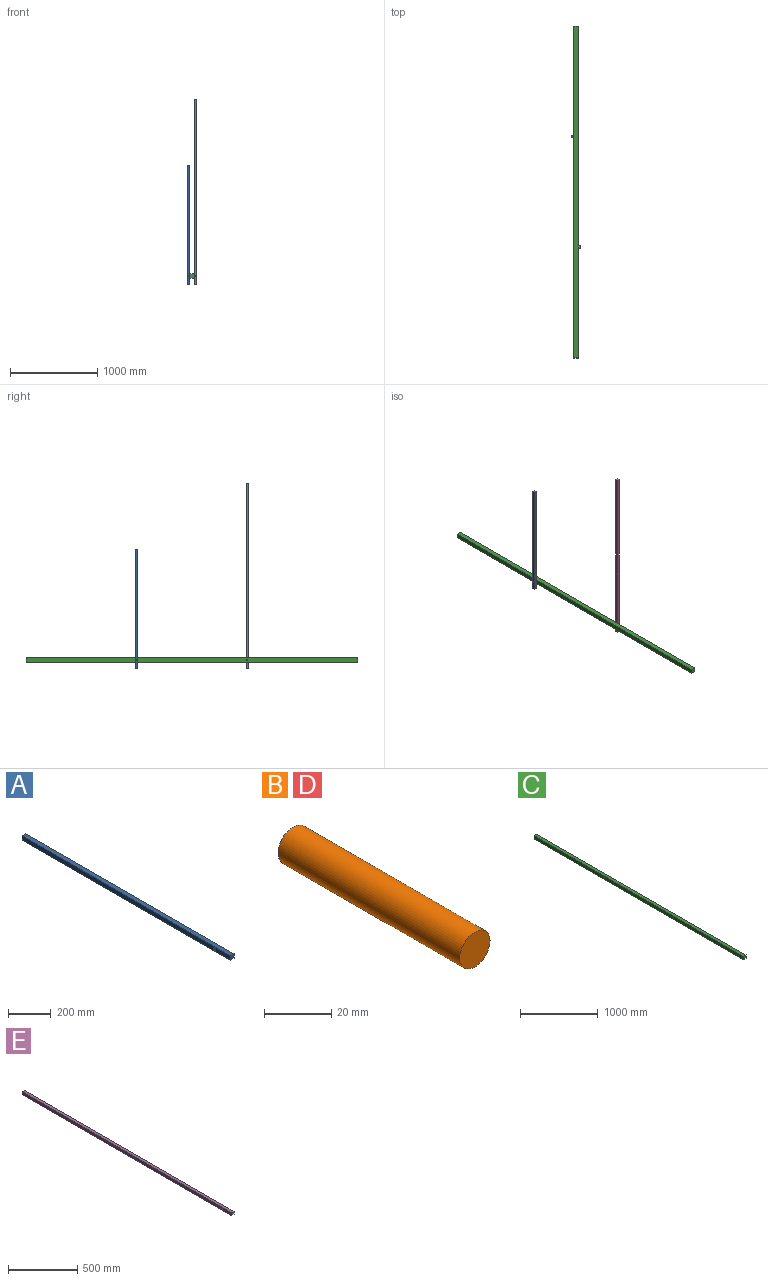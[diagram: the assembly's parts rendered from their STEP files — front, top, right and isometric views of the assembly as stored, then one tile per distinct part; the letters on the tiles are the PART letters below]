
ASSEMBLY  parts=5 mates=9
PART A: 7 faces, bbox 25.4x1371.6x25.4 mm
  f0: plane 1371.6x25.4mm, normal (0,0,1), area 34838.6mm2, adj f1,f3,f4,f5
  f1: plane 1371.6x25.4mm, normal (-1,0,0), area 34695.7mm2, adj f0,f2,f4,f5,f6
  f2: plane 1371.6x25.4mm, normal (0,0,-1), area 34838.6mm2, adj f1,f3,f4,f5
  f3: plane 1371.6x25.4mm, normal (1,0,0), area 34695.7mm2, adj f0,f2,f4,f5,f6
  f4: plane 25.4x25.4mm, normal (0,-1,0), area 645.2mm2, adj f0,f1,f2,f3
  f5: plane 25.4x25.4mm, normal (0,1,0), area 645.2mm2, adj f0,f1,f2,f3
  f6: cylinder r=6.75mm len=25.4mm, axis (1,0,0), area 1076.7mm2, adj f1,f3
PART B: 3 faces, bbox 12.7x76.2x12.7 mm
  f0: cylinder r=6.35mm len=76.2mm, axis (0,1,0), area 3040.2mm2, adj f1,f2
  f1: plane 12.7x12.7mm, normal (0,-1,0), area 126.7mm2, adj f0
  f2: plane 12.7x12.7mm, normal (0,1,0), area 126.7mm2, adj f0
PART C: 8 faces, bbox 50.8x3810x50.8 mm
  f0: plane 3810x50.8mm, normal (-1,0,0), area 193262mm2, adj f1,f3,f4,f5,f6,f7
  f1: plane 3810x50.8mm, normal (0,0,-1), area 193548mm2, adj f0,f2,f4,f5
  f2: plane 3810x50.8mm, normal (1,0,0), area 193262mm2, adj f1,f3,f4,f5,f6,f7
  f3: plane 3810x50.8mm, normal (0,0,1), area 193548mm2, adj f0,f2,f4,f5
  f4: plane 50.8x50.8mm, normal (0,-1,0), area 2580.6mm2, adj f0,f1,f2,f3
  f5: plane 50.8x50.8mm, normal (0,1,0), area 2580.6mm2, adj f0,f1,f2,f3
  f6: cylinder r=6.75mm len=50.8mm, axis (1,0,0), area 2153.3mm2, adj f0,f2
  f7: cylinder r=6.75mm len=50.8mm, axis (1,0,0), area 2153.3mm2, adj f0,f2
PART D: same geometry as B
PART E: 7 faces, bbox 25.4x2133.6x25.4 mm
  f0: plane 2133.6x25.4mm, normal (0,0,1), area 54193.4mm2, adj f1,f3,f4,f5
  f1: plane 2133.6x25.4mm, normal (-1,0,0), area 54050.5mm2, adj f0,f2,f4,f5,f6
  f2: plane 2133.6x25.4mm, normal (0,0,-1), area 54193.4mm2, adj f1,f3,f4,f5
  f3: plane 2133.6x25.4mm, normal (1,0,0), area 54050.5mm2, adj f0,f2,f4,f5,f6
  f4: plane 25.4x25.4mm, normal (0,-1,0), area 645.2mm2, adj f0,f1,f2,f3
  f5: plane 25.4x25.4mm, normal (0,1,0), area 645.2mm2, adj f0,f1,f2,f3
  f6: cylinder r=6.75mm len=25.4mm, axis (1,0,0), area 1076.7mm2, adj f1,f3
PLACE A rot(axis=(0,0.71,0.71),180deg) t=(-1250.96,-537.81,562.1)mm
PLACE B rot(axis=(0,0,-1),90deg) t=(-1154.16,-1805.99,-707.9)mm
PLACE C t=(-1204.54,738.54,-707.9)mm
PLACE D rot(axis=(0.58,0.58,-0.58),120deg) t=(-1179.56,-531.46,-712.43)mm
PLACE E rot(axis=(0,0.71,0.71),180deg) t=(-1174.76,-1807.81,1324.1)mm
MATE parallel A.f5 <-> C.f3  axis (0,0,1) through (-1243.06,-531.46,562.1)mm
MATE cylindrical D.f0 <-> C.f6  axis (1,0,0) through (-1217.66,-531.46,-707.9)mm
MATE planar B.f0 <-> E.f1  axis (1,0,0) through (-1154.16,-1801.46,-707.9)mm
MATE revolute E.f6 <-> C.f7  axis (-1,0,0) through (-1179.56,-1801.46,-707.9)mm
MATE cylindrical B.f0 <-> E.f6  axis (1,0,0) through (-1192.26,-1801.46,-707.9)mm
MATE planar A.f1 <-> C.f0  axis (1,0,0) through (-1230.36,-531.46,-121.29)mm
MATE planar D.f0 <-> C.f2  axis (1,0,0) through (-1179.56,-531.46,-707.9)mm
MATE cylindrical A.f6 <-> C.f6  axis (1,0,0) through (-1230.36,-531.46,-707.9)mm
MATE parallel E.f5 <-> C.f3  axis (0,0,1) through (-1166.86,-1801.46,1324.1)mm
